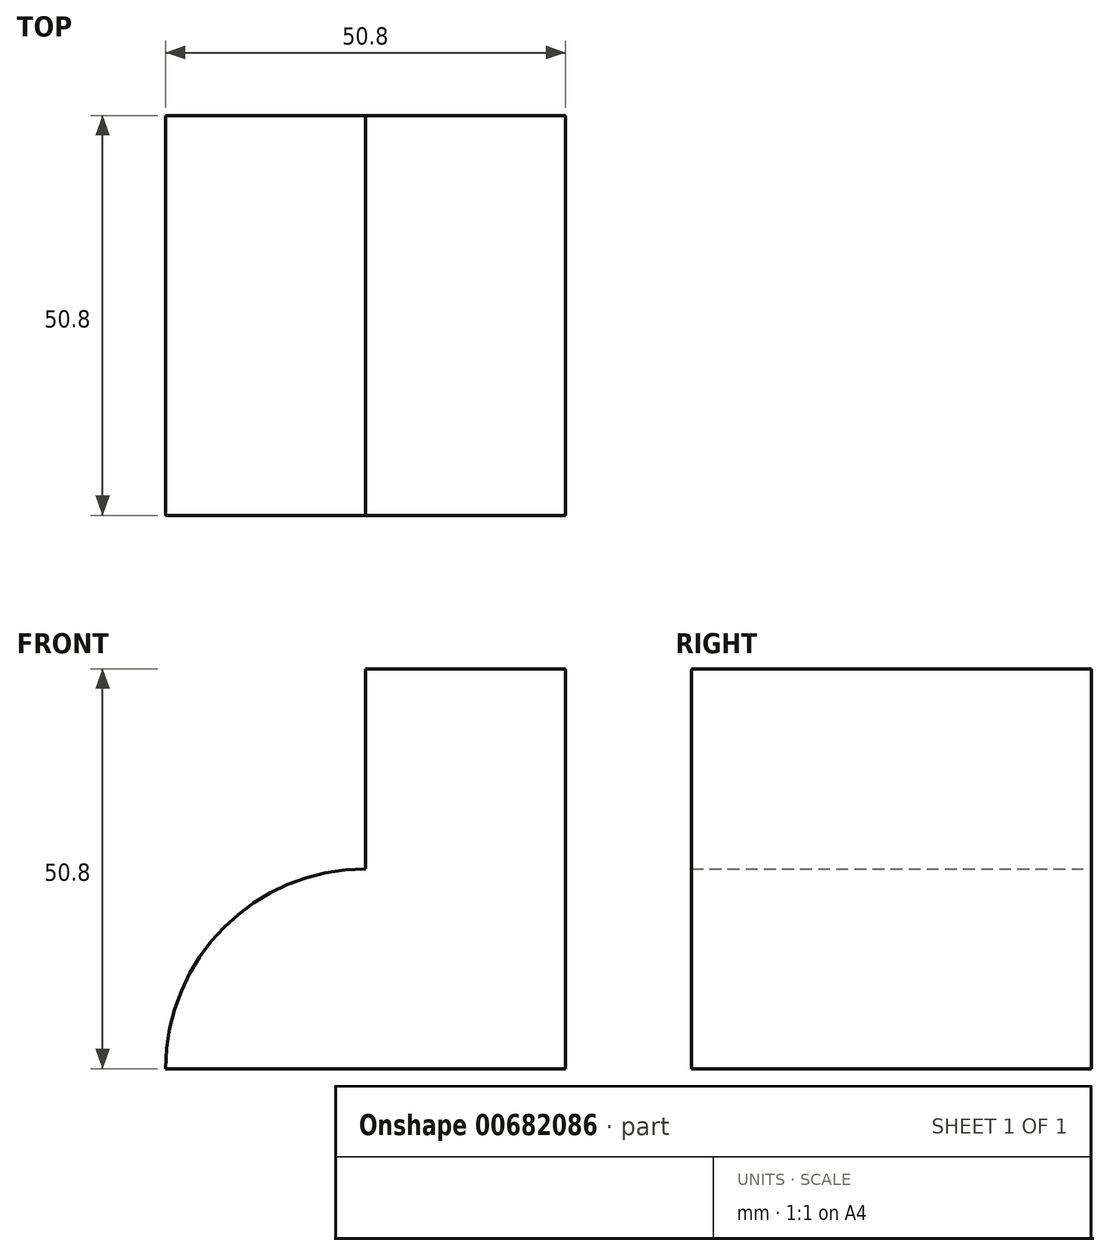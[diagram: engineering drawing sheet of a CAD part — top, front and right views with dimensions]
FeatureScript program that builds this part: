
annotation { "Feature Type Name" : "Feature", "Feature Type Description" : "" }
export const myFeature = defineFeature(function(context is Context, id is Id, definition is map)
    precondition{}
    {
        {
            var Q0;
            Q0=qCreatedBy(makeId("Front.planeOp"),FACE);
            var sketch = newSketch(context, id + "F0", { "sketchPlane" : qUnion([Q0])});
            skLineSegment(sketch, "E0", {"start": v(0, 0) * mm, "end": v(50.8, 0) * mm});
            skLineSegment(sketch, "E1", {"start": v(50.8, 0) * mm, "end": v(50.8, 50.8) * mm});
            skLineSegment(sketch, "E2", {"start": v(50.8, 50.8) * mm, "end": v(25.4, 50.8) * mm});
            skLineSegment(sketch, "E3", {"start": v(25.4, 50.8) * mm, "end": v(25.4, 25.4) * mm});
            skArc(sketch, "E4", {"start": v(25.4, 25.4) * mm, "mid": v(7.45, 17.95) * mm, "end": v(0, 0) * mm});
            skSolve(sketch);
        }
        {
            var Q0;
            Q0 = qSketchRegion(id + "F0", true);
            extrude(context, id + "F1", {"entities" : qUnion([Q0]), "depth" : 50.8 * mm, "offsetDistance" : 25.4 * mm});
        }
    });
